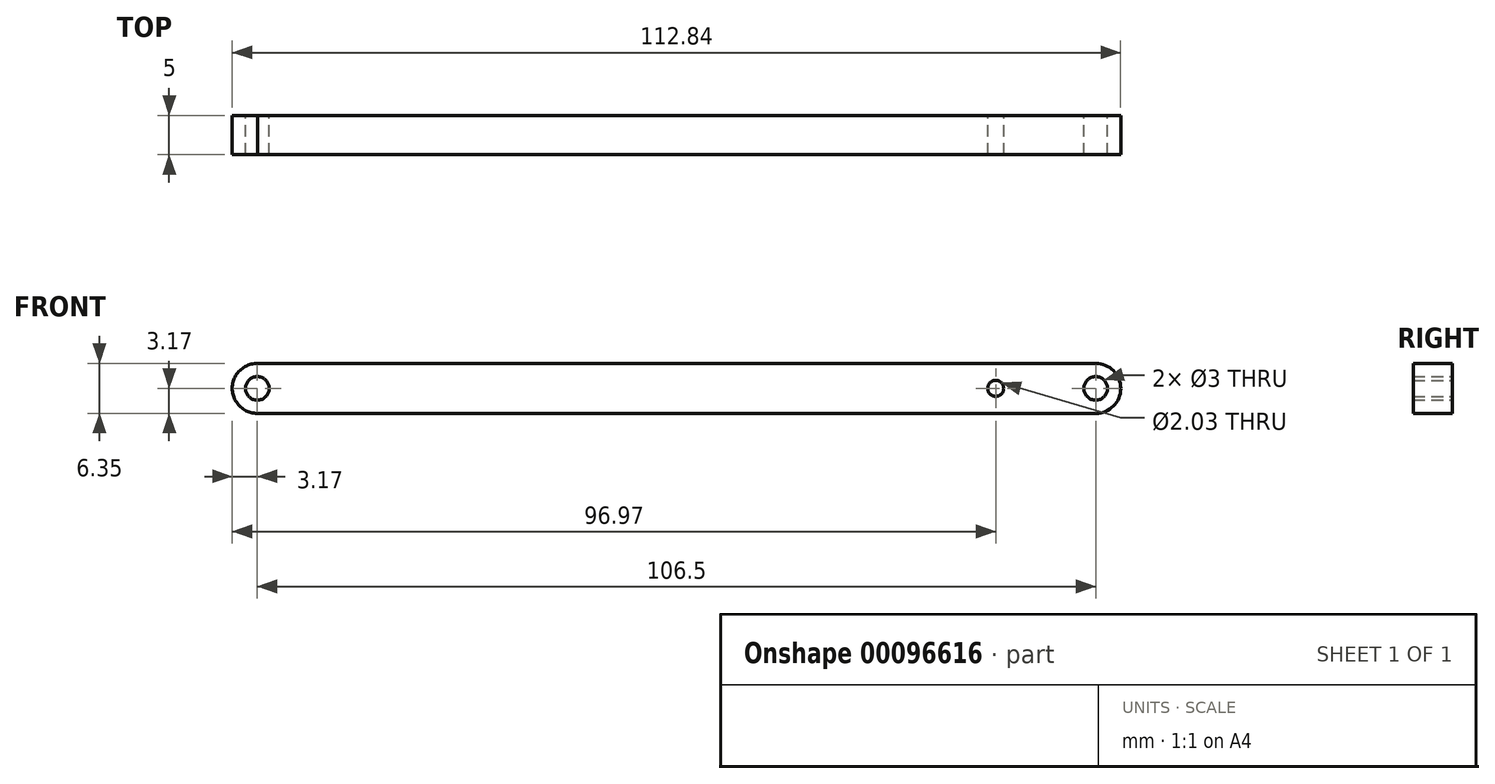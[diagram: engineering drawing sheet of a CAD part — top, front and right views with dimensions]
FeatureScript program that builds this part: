
annotation { "Feature Type Name" : "Feature", "Feature Type Description" : "" }
export const myFeature = defineFeature(function(context is Context, id is Id, definition is map)
    precondition{}
    {
        {
            var Q0;
            Q0=qCreatedBy(makeId("Front.planeOp"),FACE);
            var sketch = newSketch(context, id + "F0", { "sketchPlane" : qUnion([Q0])});
            skCircle(sketch, "E0", {"center": v(0, 0) * mm, "radius": 1.5 * mm});
            skCircle(sketch, "E1", {"center": v(0, 0) * mm, "radius": 3.18 * mm});
            skLineSegment(sketch, "E2", {"start": v(0, 0) * mm, "end": v(-106.5, 0) * mm});
            skLineSegment(sketch, "E3", {"start": v(-106.5, 0) * mm, "end": v(0, 0) * mm});
            skCircle(sketch, "E4", {"center": v(-106.5, 0) * mm, "radius": 1.5 * mm});
            skCircle(sketch, "E5", {"center": v(-106.5, 0) * mm, "radius": 3.18 * mm});
            skLineSegment(sketch, "E6", {"start": v(-106.45, 3.17) * mm, "end": v(0, 3.18) * mm});
            skLineSegment(sketch, "E7", {"start": v(0, 3.18) * mm, "end": v(-106.45, 3.17) * mm});
            skLineSegment(sketch, "E8", {"start": v(-106.5, -3.18) * mm, "end": v(0, -3.18) * mm});
            skLineSegment(sketch, "E9", {"start": v(0, -3.17) * mm, "end": v(-106.5, -3.18) * mm});
            skSolve(sketch);
        }
        {
            var Q0;
            Q0 = qSketchRegion(id + "F0", true);
            extrude(context, id + "F1", {"entities" : qUnion([Q0]), "depth" : 5 * mm});
        }
        {
            var Q0;
            Q0=qCreatedBy(makeId("Front.planeOp"),FACE);
            var sketch = newSketch(context, id + "F2", { "sketchPlane" : qUnion([Q0])});
            skLineSegment(sketch, "E10", {"start": v(0, 0) * mm, "end": v(-12.7, 0) * mm});
            skLineSegment(sketch, "E11", {"start": v(-12.7, 0) * mm, "end": v(0, 0) * mm});
            skCircle(sketch, "E12", {"center": v(-12.7, 0) * mm, "radius": 1.02 * mm});
            skSolve(sketch);
        }
        {
            var Q0;
            Q0 = qSketchRegion(id + "F2", true);
            extrude(context, id + "F3", {"entities" : qUnion([Q0]), "operationType" : NewBodyOperationType.REMOVE, "depth" : 25.4 * mm});
        }
    });
